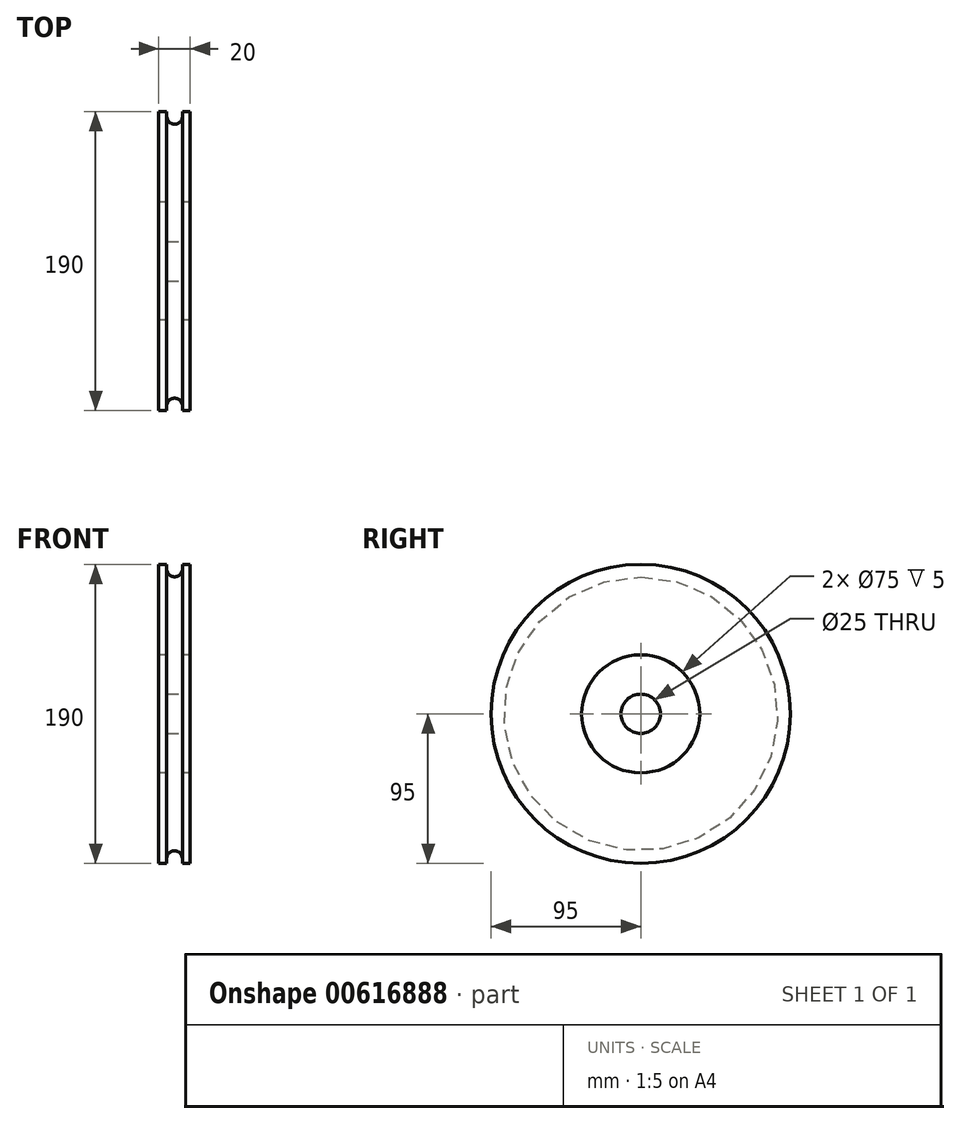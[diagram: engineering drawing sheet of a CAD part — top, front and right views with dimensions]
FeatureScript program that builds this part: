
annotation { "Feature Type Name" : "Feature", "Feature Type Description" : "" }
export const myFeature = defineFeature(function(context is Context, id is Id, definition is map)
    precondition{}
    {
        {
            var Q0;
            Q0=qCreatedBy(makeId("Front.planeOp"),FACE);
            var sketch = newSketch(context, id + "F0", { "sketchPlane" : qUnion([Q0])});
            skLineSegment(sketch, "E0", {"start": v(0, 37.5) * mm, "end": v(0, 95) * mm});
            skLineSegment(sketch, "E1", {"start": v(0, 95) * mm, "end": v(5, 95) * mm});
            skLineSegment(sketch, "E2", {"start": v(5, 95) * mm, "end": v(5, 92) * mm});
            skLineSegment(sketch, "E3", {"start": v(15, 92) * mm, "end": v(15, 95) * mm});
            skLineSegment(sketch, "E4", {"start": v(15, 95) * mm, "end": v(20, 95) * mm});
            skLineSegment(sketch, "E5", {"start": v(20, 95) * mm, "end": v(20, 37.5) * mm});
            skLineSegment(sketch, "E6", {"start": v(20, 37.5) * mm, "end": v(0, 37.5) * mm});
            skArc(sketch, "E7", {"start": v(5, 92) * mm, "mid": v(10, 87) * mm, "end": v(15, 92) * mm});
            skLineSegment(sketch, "E8", {"start": v(0, 0) * mm, "end": v(56.3, 0) * mm, "construction": true});
            skSolve(sketch);
        }
        {
            var Q0;
            Q0 = qSketchRegion(id + "F0", true);
            var Q1;
            Q1=sQuery(id+"F0.wireOp",EDGE,"E8");
            revolve(context, id + "F1", {"surfaceOperationType" : NewSurfaceOperationType.NEW, "entities" : qUnion([Q0]), "axis" : qUnion([Q1]), "revolveType" : RevolveType.FULL});
        }
        {
            var Q0;
            Q0=makeQuery(id+"F1.opRevolve","SWEPT_FACE",FACE,{"disambiguationData":[OSD([sQuery(id+"F0.wireOp",EDGE,"E5")])]});
            var sketch = newSketch(context, id + "F2", { "sketchPlane" : qUnion([Q0])});
            skCircle(sketch, "E9", {"center": v(0, 0) * mm, "radius": 12.5 * mm});
            skCircle(sketch, "E10.0", {"center": v(0, 0) * mm, "radius": 37.5 * mm});
            skSolve(sketch);
        }
        {
            var Q0;
            Q0 = qSketchRegion(id + "F2", true);
            extrude(context, id + "F3", {"entities" : qUnion([Q0]), "operationType" : NewBodyOperationType.ADD, "oppositeDirection" : true, "depth" : 15 * mm, "offsetDistance" : 25 * mm, "hasSecondDirection" : true, "secondDirectionOppositeDirection" : true, "secondDirectionDepth" : 5 * mm});
        }
    });
